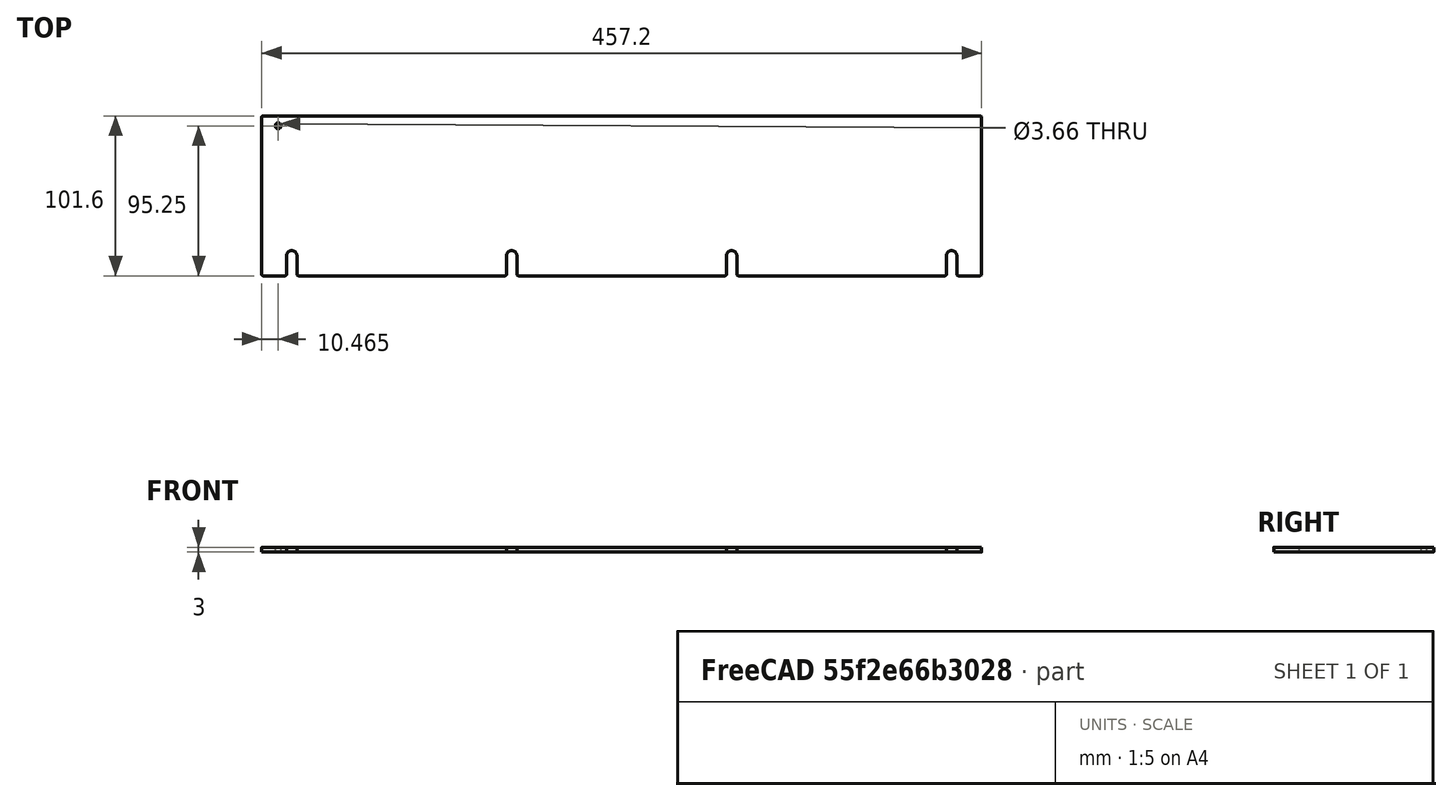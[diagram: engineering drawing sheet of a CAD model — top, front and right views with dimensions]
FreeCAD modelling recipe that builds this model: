
FCSTD DOCUMENT  (FreeCAD 0.21R33675 (Git))
Label: plain_wall_18in
License: All rights reserved
LicenseURL: http://en.wikipedia.org/wiki/All_rights_reserved
objects: Sketcher::SketchObject×1, Spreadsheet::Sheet×1, PartDesign::Pad×1, PartDesign::Body×1
note: 4 computed .brp shape members not serialized (recipe doc carries the construction recipe); baked Part::Feature solids carry a one-line shape summary decoded from their .brp

FEATURE [Sketcher::SketchObject] Sketch
  FullyConstrained = true
  MapMode = 5
  Support = -> [XY_Plane]
  expr: Constraints[122] = Spreadsheet.BracketHoleFromSide
  expr: Constraints[125] = Spreadsheet.UpperBracketHoleFromTop
  expr: Constraints[127] = Spreadsheet.BracketHoleDiameter
  expr: Constraints[19] = Spreadsheet.FilletRadius
  expr: Constraints[21] = Spreadsheet.Height
  expr: Constraints[22] = Spreadsheet.Length
  expr: Constraints[27] = Spreadsheet.MountHoleDistanceFromBottom
  expr: Constraints[29] = Spreadsheet.MountHoleDiameter
  expr: Constraints[49] = Spreadsheet.MountHoleSideMargin
  expr: Constraints[53] = Spreadsheet.MountHoleDistanceFromBottom
  sketch-geometry (49):
    g0: ArcOfCircle CenterX=-227.6 CenterY=49.8 CenterZ=0 NormalX=0 NormalY=0 NormalZ=1 AngleXU=0 Radius=1 StartAngle=1.5708 EndAngle=3.14159
    g1: LineSegment StartX=-227.6 StartY=50.8 StartZ=0 EndX=227.6 EndY=50.8 EndZ=0
    g2: ArcOfCircle CenterX=227.6 CenterY=49.8 CenterZ=0 NormalX=0 NormalY=0 NormalZ=1 AngleXU=0 Radius=1 StartAngle=-9e-16 EndAngle=1.5708
    g3: LineSegment StartX=228.6 StartY=49.8 StartZ=0 EndX=228.6 EndY=-49.8 EndZ=0
    g4: ArcOfCircle CenterX=227.6 CenterY=-49.8 CenterZ=0 NormalX=0 NormalY=0 NormalZ=1 AngleXU=0 Radius=1 StartAngle=4.71239 EndAngle=6.28319
    g5: LineSegment StartX=227.6 StartY=-50.8 StartZ=0 EndX=-227.6 EndY=-50.8 EndZ=0
    g6: ArcOfCircle CenterX=-227.6 CenterY=-49.8 CenterZ=0 NormalX=0 NormalY=0 NormalZ=1 AngleXU=0 Radius=1 StartAngle=3.14159 EndAngle=4.71239
    g7: LineSegment StartX=-228.6 StartY=-49.8 StartZ=0 EndX=-228.6 EndY=49.8 EndZ=0
    g8: GeomPoint X=-228.6 Y=50.8 Z=0
    g9: GeomPoint X=228.6 Y=-50.8 Z=0
    g10: LineSegment StartX=-69.85 StartY=-38.1 StartZ=0 EndX=69.85 EndY=-38.1 EndZ=0
    g11: LineSegment StartX=0 StartY=-50.8 StartZ=0 EndX=0 EndY=-38.1 EndZ=0
    g12: Circle CenterX=-69.85 CenterY=-38.1 CenterZ=0 NormalX=0 NormalY=0 NormalZ=1 AngleXU=0 Radius=3.302
    g13: Circle CenterX=69.85 CenterY=-38.1 CenterZ=0 NormalX=0 NormalY=0 NormalZ=1 AngleXU=0 Radius=3.302
    g14: LineSegment StartX=-69.85 StartY=-38.1 StartZ=0 EndX=-209.55 EndY=-38.1 EndZ=0
    g15: LineSegment StartX=-209.55 StartY=-38.1 StartZ=0 EndX=-228.6 EndY=-38.1 EndZ=0
    g16: LineSegment StartX=69.85 StartY=-38.1 StartZ=0 EndX=209.55 EndY=-38.1 EndZ=0
    g17: LineSegment StartX=209.55 StartY=-38.1 StartZ=0 EndX=228.6 EndY=-38.1 EndZ=0
    g18: Circle CenterX=-209.55 CenterY=-38.1 CenterZ=0 NormalX=0 NormalY=0 NormalZ=1 AngleXU=0 Radius=3.302
    g19: Circle CenterX=209.55 CenterY=-38.1 CenterZ=0 NormalX=0 NormalY=0 NormalZ=1 AngleXU=0 Radius=3.302
    g20: LineSegment StartX=0 StartY=-38.1 StartZ=0 EndX=0 EndY=-50.8 EndZ=0
    g21: ArcOfCircle CenterX=-209.55 CenterY=-38.1 CenterZ=0 NormalX=0 NormalY=0 NormalZ=1 AngleXU=0 Radius=3.302 StartAngle=-9e-16 EndAngle=3.14159
    g22: LineSegment StartX=-212.852 StartY=-38.1 StartZ=0 EndX=-212.852 EndY=-49.8 EndZ=0
    g23: LineSegment StartX=-206.248 StartY=-38.1 StartZ=0 EndX=-206.248 EndY=-49.8 EndZ=0
    g24: ArcOfCircle CenterX=-213.852 CenterY=-49.8 CenterZ=0 NormalX=0 NormalY=0 NormalZ=1 AngleXU=0 Radius=1 StartAngle=4.71239 EndAngle=6.28319
    g25: ArcOfCircle CenterX=-205.248 CenterY=-49.8 CenterZ=0 NormalX=0 NormalY=0 NormalZ=1 AngleXU=0 Radius=1 StartAngle=3.14159 EndAngle=4.71239
    g26: ArcOfCircle CenterX=-65.548 CenterY=-49.8 CenterZ=0 NormalX=0 NormalY=0 NormalZ=1 AngleXU=0 Radius=1 StartAngle=3.14159 EndAngle=4.71239
    g27: LineSegment StartX=-66.548 StartY=-38.1 StartZ=0 EndX=-66.548 EndY=-49.8 EndZ=0
    g28: ArcOfCircle CenterX=-69.85 CenterY=-38.1 CenterZ=0 NormalX=0 NormalY=0 NormalZ=1 AngleXU=0 Radius=3.302 StartAngle=-1.8e-15 EndAngle=3.14159
    g29: LineSegment StartX=-73.152 StartY=-38.1 StartZ=0 EndX=-73.152 EndY=-49.8 EndZ=0
    g30: ArcOfCircle CenterX=-74.152 CenterY=-49.8 CenterZ=0 NormalX=0 NormalY=0 NormalZ=1 AngleXU=0 Radius=1 StartAngle=4.71239 EndAngle=6.28319
    g31: ArcOfCircle CenterX=65.548 CenterY=-49.8 CenterZ=0 NormalX=0 NormalY=0 NormalZ=1 AngleXU=0 Radius=1 StartAngle=4.71239 EndAngle=6.28319
    g32: ArcOfCircle CenterX=74.152 CenterY=-49.8 CenterZ=0 NormalX=0 NormalY=0 NormalZ=1 AngleXU=0 Radius=1 StartAngle=3.14159 EndAngle=4.71239
    g33: LineSegment StartX=73.152 StartY=-38.1 StartZ=0 EndX=73.152 EndY=-49.8 EndZ=0
    g34: LineSegment StartX=66.548 StartY=-38.1 StartZ=0 EndX=66.548 EndY=-49.8 EndZ=0
    g35: ArcOfCircle CenterX=69.85 CenterY=-38.1 CenterZ=0 NormalX=0 NormalY=0 NormalZ=1 AngleXU=0 Radius=3.302 StartAngle=-1.8e-15 EndAngle=3.14159
    g36: ArcOfCircle CenterX=205.248 CenterY=-49.8 CenterZ=0 NormalX=0 NormalY=0 NormalZ=1 AngleXU=0 Radius=1 StartAngle=4.71239 EndAngle=6.28319
    g37: ArcOfCircle CenterX=213.852 CenterY=-49.8 CenterZ=0 NormalX=0 NormalY=0 NormalZ=1 AngleXU=0 Radius=1 StartAngle=3.14159 EndAngle=4.71239
    g38: LineSegment StartX=212.852 StartY=-38.1 StartZ=0 EndX=212.852 EndY=-49.8 EndZ=0
    g39: LineSegment StartX=206.248 StartY=-38.1 StartZ=0 EndX=206.248 EndY=-49.8 EndZ=0
    g40: ArcOfCircle CenterX=209.55 CenterY=-38.1 CenterZ=0 NormalX=0 NormalY=0 NormalZ=1 AngleXU=0 Radius=3.302 StartAngle=-2.7e-15 EndAngle=3.14159
    g41: LineSegment StartX=-227.6 StartY=-50.8 StartZ=0 EndX=-213.852 EndY=-50.8 EndZ=0
    g42: LineSegment StartX=-205.248 StartY=-50.8 StartZ=0 EndX=-74.152 EndY=-50.8 EndZ=0
    g43: LineSegment StartX=-65.548 StartY=-50.8 StartZ=0 EndX=65.548 EndY=-50.8 EndZ=0
    g44: LineSegment StartX=74.152 StartY=-50.8 StartZ=0 EndX=205.248 EndY=-50.8 EndZ=0
    g45: LineSegment StartX=213.852 StartY=-50.8 StartZ=0 EndX=227.6 EndY=-50.8 EndZ=0
    g46: LineSegment StartX=-228.6 StartY=50.8 StartZ=0 EndX=-218.135 EndY=50.8 EndZ=0
    g47: LineSegment StartX=-218.135 StartY=50.8 StartZ=0 EndX=-218.135 EndY=44.45 EndZ=0
    g48: Circle CenterX=-218.135 CenterY=44.45 CenterZ=0 NormalX=0 NormalY=0 NormalZ=1 AngleXU=0 Radius=1.8288
  constraints (128):
    c: Tangent(g0,g1) = 1.5708
    c: Tangent(g1,g2) = 1.5708
    c: Tangent(g2,g3) = 1.5708
    c: Tangent(g3,g4) = 1.5708
    c: Tangent(g4,g5) = 1.5708
    c: Tangent(g5,g6) = 1.5708
    c: Tangent(g6,g7) = 1.5708
    c: Tangent(g7,g0) = 1.5708
    c: Horizontal(g1)
    c: Horizontal(g5)
    c: Vertical(g3)
    c: Vertical(g7)
    c: Equal(g0,g2)
    c: Equal(g2,g4)
    c: Equal(g4,g6)
    c: PointOnObject(g8,g1)
    c: PointOnObject(g8,g7)
    c: PointOnObject(g9,g3)
    c: PointOnObject(g9,g5)
    c: Radius(g2) = 1
    c: Symmetric(g8,g9,g-1)
    c: DistanceY(g4,g1) = 101.6
    c: DistanceX(g0,g2) = 457.2
    c: Horizontal(g10)
    c: Vertical(g11)
    c: PointOnObject(g11,g5)
    c: PointOnObject(g11,g-2)
    c: DistanceY(g11,g11) = 12.7
    c: Coincident(g13,g10)
    c: Diameter(g13) = 6.604
    c: Equal(g12,g13)
    c: Coincident(g12,g10)
    c: Coincident(g14,g12)
    c: Horizontal(g14)
    c: Coincident(g15,g14)
    c: PointOnObject(g15,g7)
    c: Horizontal(g15)
    c: Coincident(g16,g13)
    c: Horizontal(g16)
    c: Coincident(g17,g16)
    c: PointOnObject(g17,g3)
    c: Horizontal(g17)
    c: Equal(g17,g15)
    c: Equal(g14,g10)
    c: Equal(g10,g16)
    c: Coincident(g18,g14)
    c: Coincident(g19,g16)
    c: Equal(g18,g12)
    c: Equal(g13,g19)
    c: DistanceX(g15,g15) = 19.05
    c: PointOnObject(g20,g10)
    c: Vertical(g20)
    c: Coincident(g20,g11)
    c: DistanceY(g20,g20) = 12.7
    c: Coincident(g21,g14)
    c: PointOnObject(g21,g15)
    c: PointOnObject(g21,g14)
    c: PointOnObject(g21,g18)
    c: Coincident(g22,g21)
    c: Vertical(g22)
    c: Coincident(g23,g21)
    c: Vertical(g23)
    c: Equal(g22,g23)
    c: Tangent(g24,g22) = 1.5708
    c: Tangent(g24,g5) = 1.5708
    c: Tangent(g25,g23) = -1.5708
    c: Tangent(g25,g5) = 1.5708
    c: Equal(g24,g6)
    c: Coincident(g29,g28)
    c: Vertical(g29)
    c: Coincident(g27,g28)
    c: Vertical(g27)
    c: Equal(g29,g27)
    c: Tangent(g30,g29) = 1.5708
    c: Tangent(g26,g27) = -1.5708
    c: PointOnObject(g28,g14)
    c: PointOnObject(g27,g10)
    c: Coincident(g28,g10)
    c: Tangent(g30,g5) = 1.5708
    c: Tangent(g26,g5) = 1.5708
    c: PointOnObject(g28,g12)
    c: Equal(g30,g25)
    c: Coincident(g34,g35)
    c: Vertical(g34)
    c: Coincident(g33,g35)
    c: Vertical(g33)
    c: Equal(g34,g33)
    c: Tangent(g31,g34) = 1.5708
    c: Tangent(g32,g33) = -1.5708
    c: PointOnObject(g33,g16)
    c: PointOnObject(g34,g10)
    c: PointOnObject(g34,g13)
    c: Tangent(g31,g5) = 1.5708
    c: Tangent(g32,g5) = 1.5708
    c: Coincident(g35,g10)
    c: Equal(g31,g4)
    c: Coincident(g39,g40)
    c: Vertical(g39)
    c: Coincident(g38,g40)
    c: Vertical(g38)
    c: Equal(g39,g38)
    c: Tangent(g36,g39) = 1.5708
    c: Tangent(g37,g38) = -1.5708
    c: PointOnObject(g38,g17)
    c: PointOnObject(g39,g16)
    c: PointOnObject(g39,g19)
    c: Coincident(g40,g16)
    c: Tangent(g36,g5) = 1.5708
    c: Tangent(g37,g5) = 1.5708
    c: Equal(g37,g4)
    c: Coincident(g41,g6)
    c: Coincident(g41,g24)
    c: Coincident(g42,g25)
    c: Coincident(g42,g30)
    c: Coincident(g43,g26)
    c: Coincident(g43,g31)
    c: Coincident(g44,g32)
    c: Coincident(g44,g36)
    c: Coincident(g45,g37)
    c: Coincident(g45,g4)
    c: Coincident(g46,g8)
    c: Horizontal(g46)
    c: DistanceX(g46,g46) = 10.4648
    c: Coincident(g47,g46)
    c: Vertical(g47)
    c: DistanceY(g47,g47) = 6.35
    c: Coincident(g48,g47)
    c: Diameter(g48) = 3.6576
FEATURE [Spreadsheet::Sheet] Spreadsheet
  cells = A2='Parameters; A3='Height; B3(Height)==4 in; A4='Length; B4(Length)==18 in; A5='Thickness; B5(Thickness)==3 mm; A6='FilletRadius; B6(FilletRadius)==1 mm; A7='MountHoleDiameter; B7(MountHoleDiameter)==0.26 in; A8='MountHoleDistanceFromBottom; B8(MountHoleDistanceFromBottom)==0.5 in; A9='MountHoleSideMargin; B9(MountHoleSideMargin)==0.75 in; A11='BracketWidth; B11(BracketWidth)==0.5 in; A12='BracketHoleDiameter; B12(BracketHoleDiameter)==0.144 in; A13='BracketHoleOffset; B13(BracketHoleOffset)==0.412 in; A14='UpperBracketHoleFromTop; B14(UpperBracketHoleFromTop)==0.5 * BracketWidth; A15='BracketHoleFromSide; B15(BracketHoleFromSide)==BracketHoleOffset
FEATURE [PartDesign::Pad] Pad
  Direction = (0,0,1)
  Length = 3
  Length2 = 10
  Profile = -> Sketch
  ReferenceAxis = -> Sketch [N_Axis]
  Type = 0
  expr: Length = Spreadsheet.Thickness
FEATURE [PartDesign::Body] Body
  Group = -> [Sketch,Pad]
  Origin = -> Origin
  Tip = -> Pad
